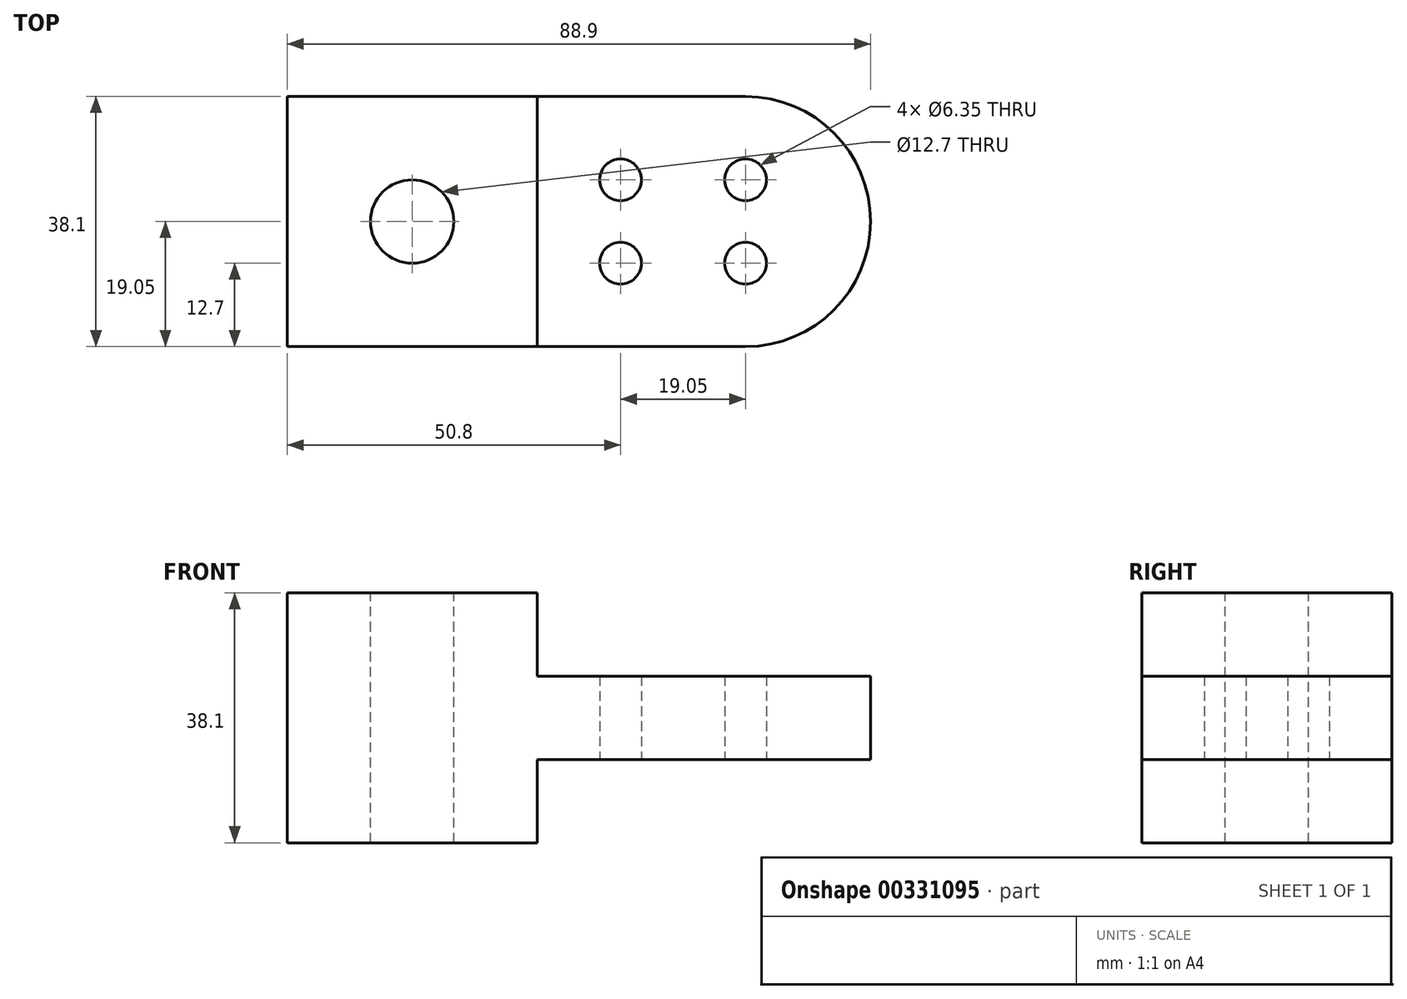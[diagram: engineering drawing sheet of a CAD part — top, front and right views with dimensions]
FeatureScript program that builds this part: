
annotation { "Feature Type Name" : "Feature", "Feature Type Description" : "" }
export const myFeature = defineFeature(function(context is Context, id is Id, definition is map)
    precondition{}
    {
        {
            var Q0;
            Q0=qCreatedBy(makeId("Top.planeOp"),FACE);
            var sketch = newSketch(context, id + "F0", { "sketchPlane" : qUnion([Q0])});
            skLineSegment(sketch, "E0", {"start": v(0, 0) * mm, "end": v(0, 38.1) * mm});
            skLineSegment(sketch, "E1", {"start": v(0, 38.1) * mm, "end": v(38.1, 38.1) * mm});
            skLineSegment(sketch, "E2", {"start": v(38.1, 38.1) * mm, "end": v(38.1, 0) * mm});
            skLineSegment(sketch, "E3", {"start": v(38.1, 0) * mm, "end": v(0, 0) * mm});
            skLineSegment(sketch, "E4", {"start": v(38.1, 38.1) * mm, "end": v(69.85, 38.1) * mm});
            skLineSegment(sketch, "E5", {"start": v(69.85, 0) * mm, "end": v(38.1, 0) * mm});
            skArc(sketch, "E6", {"start": v(69.85, 0) * mm, "mid": v(88.9, 19.05) * mm, "end": v(69.85, 38.1) * mm});
            skCircle(sketch, "E7", {"center": v(19.05, 19.05) * mm, "radius": 6.35 * mm});
            skLineSegment(sketch, "E8.bottom", {"start": v(50.8, 12.7) * mm, "end": v(69.85, 12.7) * mm, "construction": true});
            skLineSegment(sketch, "E8.top", {"start": v(50.8, 25.4) * mm, "end": v(69.85, 25.4) * mm, "construction": true});
            skLineSegment(sketch, "E8.left", {"start": v(50.8, 12.7) * mm, "end": v(50.8, 25.4) * mm, "construction": true});
            skLineSegment(sketch, "E8.right", {"start": v(69.85, 12.7) * mm, "end": v(69.85, 25.4) * mm, "construction": true});
            skCircle(sketch, "E9", {"center": v(69.85, 25.4) * mm, "radius": 3.18 * mm});
            skCircle(sketch, "E10", {"center": v(69.85, 12.7) * mm, "radius": 3.18 * mm});
            skCircle(sketch, "E11", {"center": v(50.8, 25.4) * mm, "radius": 3.18 * mm});
            skCircle(sketch, "E12", {"center": v(50.8, 12.7) * mm, "radius": 3.18 * mm});
            skSolve(sketch);
        }
        {
            var Q0;
            Q0=makeQuery(id+"F0.imprint","IMPRINT",FACE,{"disambiguationData":[TD([[makeQuery(id+"F0.imprint","IMPRINT",EDGE,{"derivedFrom":sQuery(id+"F0.wireOp",EDGE,"E0")}),-1.0]])]});
            extrude(context, id + "F1", {"entities" : qUnion([Q0]), "endBound" : BoundingType.SYMMETRIC, "oppositeDirection" : true, "depth" : 38.1 * mm});
        }
        {
            var Q0;
            Q0=makeQuery(id+"F0.imprint","IMPRINT",FACE,{"disambiguationData":[TD([[makeQuery(id+"F0.imprint","IMPRINT",EDGE,{"derivedFrom":sQuery(id+"F0.wireOp",EDGE,"E2")}),1.0]])]});
            extrude(context, id + "F2", {"entities" : qUnion([Q0]), "operationType" : NewBodyOperationType.ADD, "endBound" : BoundingType.SYMMETRIC, "depth" : 12.7 * mm});
        }
    });
